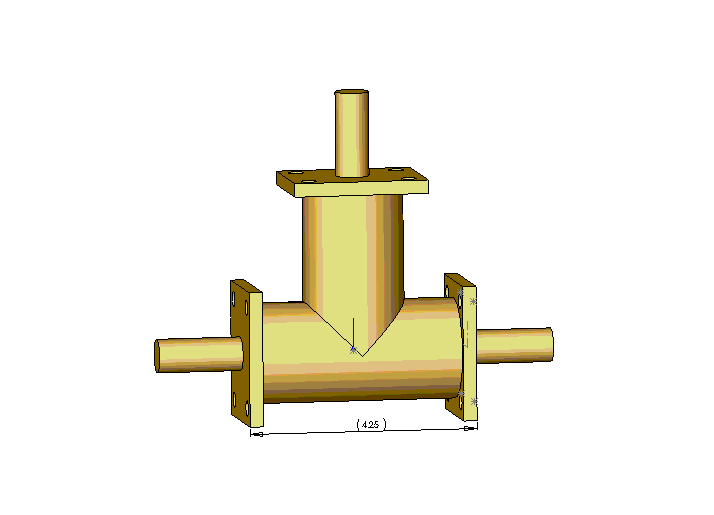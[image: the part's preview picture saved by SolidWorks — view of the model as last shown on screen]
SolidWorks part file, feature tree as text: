
SOLIDWORKS PART (.sldprt)
format: sldprt  version: not decoded by parser v0  size: 458,752 bytes
history: native  units: mm
features: sketch x14, extrude x8, hole x3 + 1 further entry (+9 scaffold rows collapsed)
feature tree (35):
  "Annotations"  RD1=107.95mm
  scaffold x9  (default folders/planes/origin — collapsed)
  sketch  "Sketch1"  dims[D1=50.8mm D2=50.8mm]
  extrude  "Extrude1"  Depth=53.975mm
  sketch  "Sketch2"  dims[D1=44.45mm]
  extrude  "Extrude2"  Depth=82.55mm
  sketch  "Sketch5"  dims[D1=63.5mm D2=50.8mm]
  extrude  "Extrude3"  Depth=6.35mm
  hole  "1/4 Clearance Hole1"  Diameter=7.14248mm Depth=6.35mm
  sketch  "Sketch4"  dims[D1=23.8125mm D2=17.4625mm D3=~38.113185mm]
  sketch  "Sketch3"  dims[hole-wizard template sketch: 60 standard entries collapsed; hole parameters kept: c18.Thru Hole Depth=6.35mm]
  sketch  "Sketch6"  dims[D1=50.8mm D2=63.5mm]
  extrude  "Extrude4"  Depth=6.35mm
  sketch  "Sketch7"
  extrude  "Extrude5"  Depth=6.35mm
  hole  "1/4 Clearance Hole2"  Diameter=7.14248mm Depth=6.35mm
  sketch  "Sketch9"  dims[D1=17.4625mm D2=23.8125mm]
  sketch  "Sketch8"  dims[hole-wizard template sketch: 60 standard entries collapsed; hole parameters kept: c18.Thru Hole Depth=6.35mm]
  hole  "1/4 Clearance Hole3"  Diameter=7.14248mm Depth=6.35mm
  sketch  "Sketch11"
  sketch  "Sketch10"  dims[hole-wizard template sketch: 60 standard entries collapsed; hole parameters kept: c18.Thru Hole Depth=6.35mm]
  sketch  "Sketch12"  dims[D1=15.875mm]
  extrude  "Extrude6"  Depth=39.7002mm
  sketch  "Sketch13"  dims[D1=15.875mm]
  extrude  "Extrude7"  Depth=39.7002mm
  sketch  "Sketch14"  dims[D1=15.875mm]
  extrude  "Extrude8"  Depth=39.7002mm
decode coverage: 23 of 25 modeling features carry decoded parameters; 1 rows unclassified (native names shown)
note: ~ marks probable driven/reference dimensions
note: suppression state not decoded; provenance and decode notes live in map.json
